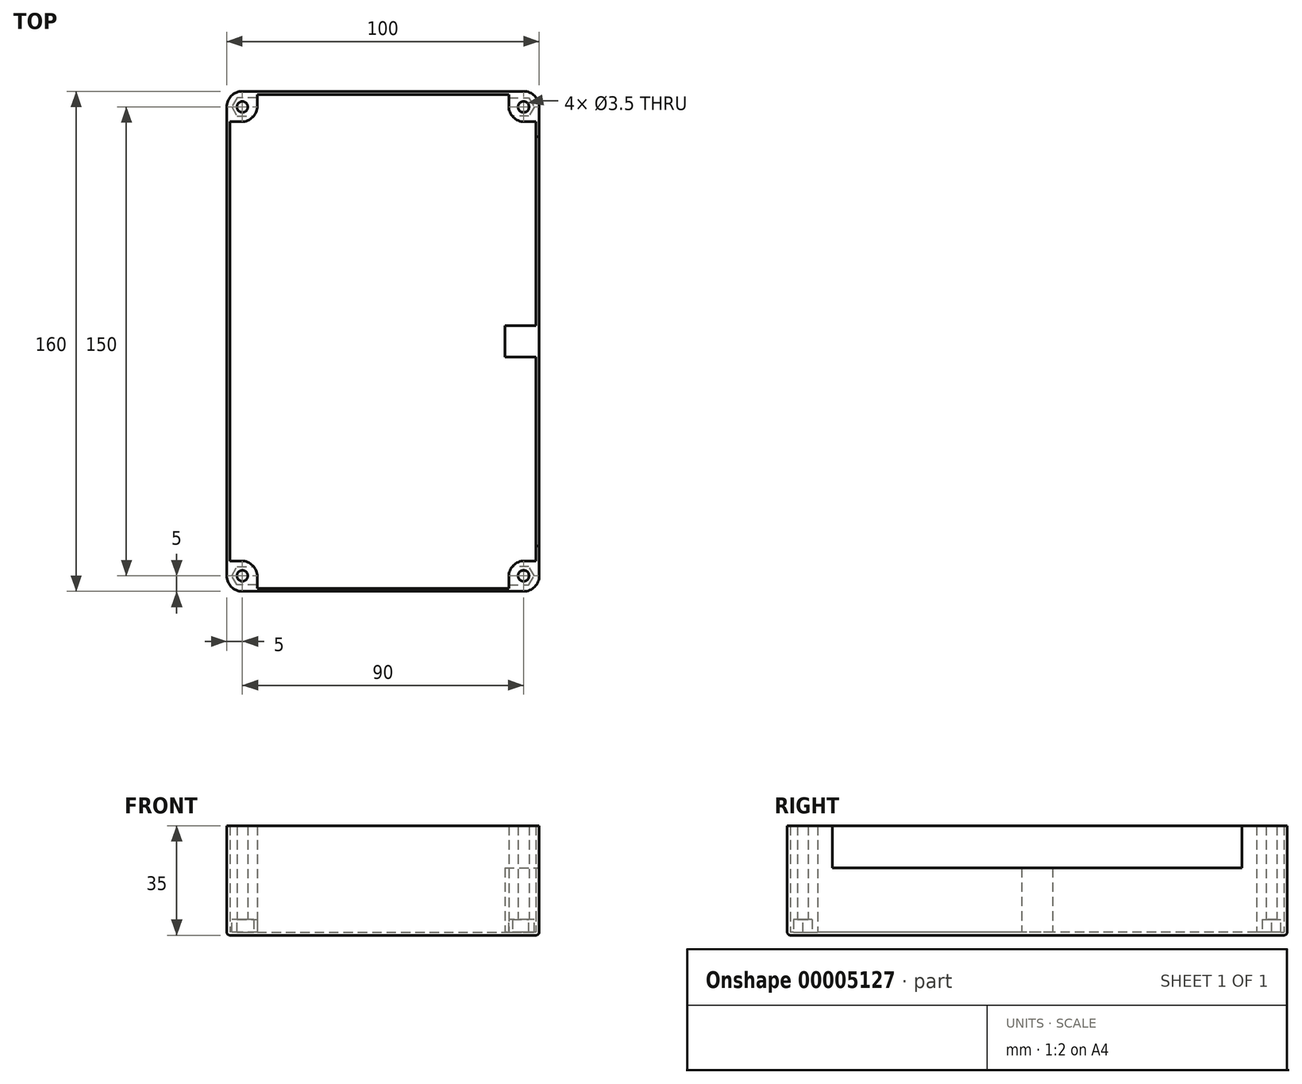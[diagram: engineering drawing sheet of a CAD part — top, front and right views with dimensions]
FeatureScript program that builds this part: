
annotation { "Feature Type Name" : "Feature", "Feature Type Description" : "" }
export const myFeature = defineFeature(function(context is Context, id is Id, definition is map)
    precondition{}
    {
        {
            var Q0;
            Q0=qCreatedBy(makeId("Top.planeOp"),FACE);
            var sketch = newSketch(context, id + "F0", { "sketchPlane" : qUnion([Q0])});
            skLineSegment(sketch, "E0.bottom", {"start": v(5, 0) * mm, "end": v(95, 0) * mm});
            skLineSegment(sketch, "E0.top", {"start": v(5, -160) * mm, "end": v(95, -160) * mm});
            skLineSegment(sketch, "E0.left", {"start": v(0, -5) * mm, "end": v(0, -155) * mm});
            skLineSegment(sketch, "E0.right", {"start": v(100, -5) * mm, "end": v(100, -155) * mm});
            skPoint(sketch, "E1.visualSharp", {"position": v(0, 0) * mm});
            skArc(sketch, "E1.filletArc", {"start": v(5, 0) * mm, "mid": v(1.46, -1.46) * mm, "end": v(0, -5) * mm});
            skPoint(sketch, "E2.visualSharp", {"position": v(0, -160) * mm});
            skArc(sketch, "E2.filletArc", {"start": v(0, -155) * mm, "mid": v(1.46, -158.54) * mm, "end": v(5, -160) * mm});
            skPoint(sketch, "E3.visualSharp", {"position": v(100, -160) * mm});
            skArc(sketch, "E3.filletArc", {"start": v(95, -160) * mm, "mid": v(98.54, -158.54) * mm, "end": v(100, -155) * mm});
            skPoint(sketch, "E4.visualSharp", {"position": v(100, 0) * mm});
            skArc(sketch, "E4.filletArc", {"start": v(100, -5) * mm, "mid": v(98.54, -1.46) * mm, "end": v(95, 0) * mm});
            skLineSegment(sketch, "E5.bottom", {"start": v(6, -1) * mm, "end": v(94, -1) * mm});
            skLineSegment(sketch, "E5.top", {"start": v(6, -159) * mm, "end": v(94, -159) * mm});
            skLineSegment(sketch, "E5.left", {"start": v(1, -6) * mm, "end": v(1, -154) * mm});
            skLineSegment(sketch, "E5.right", {"start": v(99, -6) * mm, "end": v(99, -154) * mm});
            skPoint(sketch, "E6.visualSharp", {"position": v(1, -1) * mm});
            skArc(sketch, "E6.filletArc", {"start": v(6, -1) * mm, "mid": v(2.46, -2.46) * mm, "end": v(1, -6) * mm});
            skPoint(sketch, "E7.visualSharp", {"position": v(99, -1) * mm});
            skArc(sketch, "E7.filletArc", {"start": v(99, -6) * mm, "mid": v(97.54, -2.46) * mm, "end": v(94, -1) * mm});
            skPoint(sketch, "E8.visualSharp", {"position": v(99, -159) * mm});
            skArc(sketch, "E8.filletArc", {"start": v(94, -159) * mm, "mid": v(97.54, -157.54) * mm, "end": v(99, -154) * mm});
            skPoint(sketch, "E9.visualSharp", {"position": v(1, -159) * mm});
            skArc(sketch, "E9.filletArc", {"start": v(1, -154) * mm, "mid": v(2.46, -157.54) * mm, "end": v(6, -159) * mm});
            skLineSegment(sketch, "E10", {"start": v(50, -1) * mm, "end": v(50, 0) * mm, "construction": true});
            skLineSegment(sketch, "E11", {"start": v(1, -80) * mm, "end": v(0, -80) * mm, "construction": true});
            skSolve(sketch);
        }
        {
            var Q0;
            Q0 = qSketchRegion(id + "F0", true);
            extrude(context, id + "F1", {"entities" : qUnion([Q0]), "depth" : 35 * mm});
        }
        {
            var Q0;
            Q0=qCreatedBy(makeId("Top.planeOp"),FACE);
            var sketch = newSketch(context, id + "F2", { "sketchPlane" : qUnion([Q0])});
            skLineSegment(sketch, "E12.bottom", {"start": v(5, 0) * mm, "end": v(95, 0) * mm});
            skLineSegment(sketch, "E12.top", {"start": v(5, -160) * mm, "end": v(95, -160) * mm});
            skLineSegment(sketch, "E12.left", {"start": v(0, -5) * mm, "end": v(0, -155) * mm});
            skLineSegment(sketch, "E12.right", {"start": v(100, -5) * mm, "end": v(100, -155) * mm});
            skPoint(sketch, "E13.visualSharp", {"position": v(0, 0) * mm});
            skArc(sketch, "E13.filletArc", {"start": v(5, 0) * mm, "mid": v(1.46, -1.46) * mm, "end": v(0, -5) * mm});
            skPoint(sketch, "E14.visualSharp", {"position": v(0, -160) * mm});
            skArc(sketch, "E14.filletArc", {"start": v(0, -155) * mm, "mid": v(1.46, -158.54) * mm, "end": v(5, -160) * mm});
            skPoint(sketch, "E15.visualSharp", {"position": v(100, -160) * mm});
            skArc(sketch, "E15.filletArc", {"start": v(95, -160) * mm, "mid": v(98.54, -158.54) * mm, "end": v(100, -155) * mm});
            skPoint(sketch, "E16.visualSharp", {"position": v(100, 0) * mm});
            skArc(sketch, "E16.filletArc", {"start": v(100, -5) * mm, "mid": v(98.54, -1.46) * mm, "end": v(95, 0) * mm});
            skSolve(sketch);
        }
        {
            var Q0;
            Q0 = qSketchRegion(id + "F2", true);
            extrude(context, id + "F3", {"entities" : qUnion([Q0]), "operationType" : NewBodyOperationType.ADD, "depth" : 1 * mm});
        }
        {
            var Q0;
            Q0=makeQuery(id+"F3.opExtrude","CAP_FACE",FACE,{"disambiguationData":[OSD([sQuery(id+"F2.wireOp",EDGE,"E12.bottom"),sQuery(id+"F2.wireOp",EDGE,"E12.top"),sQuery(id+"F2.wireOp",EDGE,"E12.left"),sQuery(id+"F2.wireOp",EDGE,"E12.right"),sQuery(id+"F2.wireOp",EDGE,"E13.filletArc"),sQuery(id+"F2.wireOp",EDGE,"E14.filletArc"),sQuery(id+"F2.wireOp",EDGE,"E15.filletArc"),sQuery(id+"F2.wireOp",EDGE,"E16.filletArc")])],"isStart":false});
            cPlane(context, id + "F4", {"entities" : qUnion([Q0]), "cplaneType" : CPlaneType.OFFSET, "offset" : 0 * mm, "width" : 150 * mm, "height" : 150 * mm});
        }
        {
            var Q0;
            Q0=qCreatedBy(id+"F4.planeOp",FACE);
            var sketch = newSketch(context, id + "F5", { "sketchPlane" : qUnion([Q0])});
            skLineSegment(sketch, "E17.bottom", {"start": v(4.75, -150.25) * mm, "end": v(1, -150.25) * mm});
            skLineSegment(sketch, "E17.top", {"start": v(9.75, -159) * mm, "end": v(6, -159) * mm});
            skLineSegment(sketch, "E17.left", {"start": v(9.75, -155.25) * mm, "end": v(9.75, -159) * mm});
            skLineSegment(sketch, "E17.right", {"start": v(1, -150.25) * mm, "end": v(1, -154) * mm});
            skPoint(sketch, "E18.visualSharp", {"position": v(1, -159) * mm});
            skArc(sketch, "E18.filletArc", {"start": v(1, -154) * mm, "mid": v(2.46, -157.54) * mm, "end": v(6, -159) * mm});
            skLineSegment(sketch, "E19.bottom", {"start": v(4.75, -9.75) * mm, "end": v(1, -9.75) * mm});
            skLineSegment(sketch, "E19.top", {"start": v(9.75, -1) * mm, "end": v(6, -1) * mm});
            skLineSegment(sketch, "E19.left", {"start": v(9.75, -4.75) * mm, "end": v(9.75, -1) * mm});
            skLineSegment(sketch, "E19.right", {"start": v(1, -9.75) * mm, "end": v(1, -6) * mm});
            skPoint(sketch, "E20.visualSharp", {"position": v(1, -1) * mm});
            skArc(sketch, "E20.filletArc", {"start": v(6, -1) * mm, "mid": v(2.46, -2.46) * mm, "end": v(1, -6) * mm});
            skLineSegment(sketch, "E21.bottom", {"start": v(95.25, -150.25) * mm, "end": v(99, -150.25) * mm});
            skLineSegment(sketch, "E21.top", {"start": v(90.25, -159) * mm, "end": v(94, -159) * mm});
            skLineSegment(sketch, "E21.left", {"start": v(90.25, -155.25) * mm, "end": v(90.25, -159) * mm});
            skLineSegment(sketch, "E21.right", {"start": v(99, -150.25) * mm, "end": v(99, -154) * mm});
            skLineSegment(sketch, "E22.bottom", {"start": v(95.25, -9.75) * mm, "end": v(99, -9.75) * mm});
            skLineSegment(sketch, "E22.top", {"start": v(90.25, -1) * mm, "end": v(94, -1) * mm});
            skLineSegment(sketch, "E22.left", {"start": v(90.25, -4.75) * mm, "end": v(90.25, -1) * mm});
            skLineSegment(sketch, "E22.right", {"start": v(99, -9.75) * mm, "end": v(99, -6) * mm});
            skPoint(sketch, "E23.visualSharp", {"position": v(99, -159) * mm});
            skArc(sketch, "E23.filletArc", {"start": v(94, -159) * mm, "mid": v(97.54, -157.54) * mm, "end": v(99, -154) * mm});
            skPoint(sketch, "E24.visualSharp", {"position": v(99, -1) * mm});
            skArc(sketch, "E24.filletArc", {"start": v(99, -6) * mm, "mid": v(97.54, -2.46) * mm, "end": v(94, -1) * mm});
            skCircle(sketch, "E25", {"center": v(5, -155) * mm, "radius": 1.75 * mm});
            skCircle(sketch, "E26", {"center": v(5, -5) * mm, "radius": 1.75 * mm});
            skCircle(sketch, "E27", {"center": v(95, -5) * mm, "radius": 1.75 * mm});
            skCircle(sketch, "E28", {"center": v(95, -155) * mm, "radius": 1.75 * mm});
            skLineSegment(sketch, "E29", {"start": v(5, -155) * mm, "end": v(1, -155) * mm, "construction": true});
            skLineSegment(sketch, "E30", {"start": v(95, -155) * mm, "end": v(99, -155) * mm, "construction": true});
            skLineSegment(sketch, "E31", {"start": v(5, -155) * mm, "end": v(5, -150.25) * mm, "construction": true});
            skLineSegment(sketch, "E32", {"start": v(5, -150.25) * mm, "end": v(5, -9.75) * mm, "construction": true});
            skLineSegment(sketch, "E33", {"start": v(5, -9.75) * mm, "end": v(5, -5) * mm, "construction": true});
            skPoint(sketch, "E34.visualSharp", {"position": v(9.75, -150.25) * mm});
            skArc(sketch, "E34.filletArc", {"start": v(9.75, -155.25) * mm, "mid": v(8.29, -151.71) * mm, "end": v(4.75, -150.25) * mm});
            skPoint(sketch, "E35.visualSharp", {"position": v(90.25, -150.25) * mm});
            skArc(sketch, "E35.filletArc", {"start": v(95.25, -150.25) * mm, "mid": v(91.71, -151.71) * mm, "end": v(90.25, -155.25) * mm});
            skPoint(sketch, "E36.visualSharp", {"position": v(90.25, -9.75) * mm});
            skArc(sketch, "E36.filletArc", {"start": v(90.25, -4.75) * mm, "mid": v(91.71, -8.29) * mm, "end": v(95.25, -9.75) * mm});
            skPoint(sketch, "E37.visualSharp", {"position": v(9.75, -9.75) * mm});
            skArc(sketch, "E37.filletArc", {"start": v(4.75, -9.75) * mm, "mid": v(8.29, -8.29) * mm, "end": v(9.75, -4.75) * mm});
            skLineSegment(sketch, "E38", {"start": v(5, -5) * mm, "end": v(5, -1.1) * mm, "construction": true});
            skLineSegment(sketch, "E39", {"start": v(5, -155) * mm, "end": v(5, -158.9) * mm, "construction": true});
            skSolve(sketch);
        }
        {
            var Q0;
            Q0 = qSketchRegion(id + "F5", true);
            var Q1;
            Q1=makeQuery(id+"F1.opExtrude","CAP_FACE",FACE,{"disambiguationData":[OSD([sQuery(id+"F0.wireOp",EDGE,"E0.bottom"),sQuery(id+"F0.wireOp",EDGE,"E0.top"),sQuery(id+"F0.wireOp",EDGE,"E0.left"),sQuery(id+"F0.wireOp",EDGE,"E0.right"),sQuery(id+"F0.wireOp",EDGE,"E1.filletArc"),sQuery(id+"F0.wireOp",EDGE,"E2.filletArc"),sQuery(id+"F0.wireOp",EDGE,"E3.filletArc"),sQuery(id+"F0.wireOp",EDGE,"E4.filletArc"),sQuery(id+"F0.wireOp",EDGE,"E5.bottom"),sQuery(id+"F0.wireOp",EDGE,"E5.top"),sQuery(id+"F0.wireOp",EDGE,"E5.left"),sQuery(id+"F0.wireOp",EDGE,"E5.right"),sQuery(id+"F0.wireOp",EDGE,"E6.filletArc"),sQuery(id+"F0.wireOp",EDGE,"E7.filletArc"),sQuery(id+"F0.wireOp",EDGE,"E8.filletArc"),sQuery(id+"F0.wireOp",EDGE,"E9.filletArc")])],"isStart":false});
            extrude(context, id + "F6", {"entities" : qUnion([Q0]), "operationType" : NewBodyOperationType.ADD, "endBound" : BoundingType.UP_TO_SURFACE, "endBoundEntityFace" : qUnion([Q1]), "depth" : 25 * mm});
        }
        {
            var Q0;
            Q0=qCreatedBy(makeId("Top.planeOp"),FACE);
            cPlane(context, id + "F7", {"entities" : qUnion([Q0]), "cplaneType" : CPlaneType.OFFSET, "offset" : 5 * mm, "width" : 150 * mm, "height" : 150 * mm});
        }
        {
            var Q0;
            Q0=qCreatedBy(id+"F7.planeOp",FACE);
            var sketch = newSketch(context, id + "F8", { "sketchPlane" : qUnion([Q0])});
            skCircle(sketch, "E40.cCircle", {"center": v(5, -5) * mm, "radius": 2.95 * mm, "construction": true});
            skLineSegment(sketch, "E40.0", {"start": v(3.3, -2.05) * mm, "end": v(6.7, -2.05) * mm});
            skLineSegment(sketch, "E40.3", {"start": v(6.7, -7.95) * mm, "end": v(3.3, -7.95) * mm});
            skLineSegment(sketch, "E40.4", {"start": v(3.3, -7.95) * mm, "end": v(1.6, -5) * mm});
            skLineSegment(sketch, "E40.5", {"start": v(1.6, -5) * mm, "end": v(3.3, -2.05) * mm});
            skPoint(sketch, "E40.0.midPoint", {"position": v(5, -2.05) * mm});
            skLineSegment(sketch, "E41", {"start": v(6.7, -2.05) * mm, "end": v(16.6, -2.05) * mm});
            skLineSegment(sketch, "E42", {"start": v(16.6, -2.05) * mm, "end": v(16.6, -7.95) * mm});
            skLineSegment(sketch, "E43", {"start": v(16.6, -7.95) * mm, "end": v(6.7, -7.95) * mm});
            skPoint(sketch, "E44.orphan", {"position": v(8.4, -5) * mm});
            skLineSegment(sketch, "E45", {"start": v(99, -80) * mm, "end": v(1, -80) * mm, "construction": true});
            skLineSegment(sketch, "E46", {"start": v(5, -5) * mm, "end": v(95, -5) * mm, "construction": true});
            skLineSegment(sketch, "E47", {"start": v(50, -5) * mm, "end": v(50, -91.07) * mm, "construction": true});
            skLineSegment(sketch, "E48.0.MirrorCS", {"start": v(98.4, -5) * mm, "end": v(96.7, -2.05) * mm});
            skLineSegment(sketch, "E48.1.MirrorCS", {"start": v(96.7, -2.05) * mm, "end": v(93.3, -2.05) * mm});
            skLineSegment(sketch, "E48.2.MirrorCS", {"start": v(93.3, -7.95) * mm, "end": v(96.7, -7.95) * mm});
            skCircle(sketch, "E48.3.MirrorC", {"center": v(95, -5) * mm, "radius": 2.95 * mm, "construction": true});
            skLineSegment(sketch, "E48.4.MirrorCS", {"start": v(96.7, -7.95) * mm, "end": v(98.4, -5) * mm});
            skPoint(sketch, "E48.5.MirrorP", {"position": v(95, -2.05) * mm});
            skLineSegment(sketch, "E48.6.MirrorCS", {"start": v(83.4, -2.05) * mm, "end": v(83.4, -7.95) * mm});
            skPoint(sketch, "E48.7.MirrorP", {"position": v(91.6, -5) * mm});
            skLineSegment(sketch, "E48.8.MirrorCS", {"start": v(93.3, -2.05) * mm, "end": v(83.4, -2.05) * mm});
            skLineSegment(sketch, "E48.9.MirrorCS", {"start": v(83.4, -7.95) * mm, "end": v(93.3, -7.95) * mm});
            skLineSegment(sketch, "E48.10.MirrorCS", {"start": v(95, -5) * mm, "end": v(5, -5) * mm, "construction": true});
            skLineSegment(sketch, "E49.0.MirrorCS", {"start": v(96.7, -157.95) * mm, "end": v(93.3, -157.95) * mm});
            skLineSegment(sketch, "E49.1.MirrorCS", {"start": v(93.3, -152.05) * mm, "end": v(96.7, -152.05) * mm});
            skLineSegment(sketch, "E49.2.MirrorCS", {"start": v(5, -155) * mm, "end": v(95, -155) * mm, "construction": true});
            skLineSegment(sketch, "E49.3.MirrorCS", {"start": v(3.3, -157.95) * mm, "end": v(6.7, -157.95) * mm});
            skLineSegment(sketch, "E49.4.MirrorCS", {"start": v(1.6, -155) * mm, "end": v(3.3, -157.95) * mm});
            skLineSegment(sketch, "E49.5.MirrorCS", {"start": v(96.7, -152.05) * mm, "end": v(98.4, -155) * mm});
            skLineSegment(sketch, "E49.6.MirrorCS", {"start": v(3.3, -152.05) * mm, "end": v(1.6, -155) * mm});
            skLineSegment(sketch, "E49.7.MirrorCS", {"start": v(6.7, -152.05) * mm, "end": v(3.3, -152.05) * mm});
            skCircle(sketch, "E49.8.MirrorC", {"center": v(5, -155) * mm, "radius": 2.95 * mm, "construction": true});
            skCircle(sketch, "E49.9.MirrorC", {"center": v(95, -155) * mm, "radius": 2.95 * mm, "construction": true});
            skLineSegment(sketch, "E49.10.MirrorCS", {"start": v(98.4, -155) * mm, "end": v(96.7, -157.95) * mm});
            skLineSegment(sketch, "E49.11.MirrorCS", {"start": v(6.7, -157.95) * mm, "end": v(16.6, -157.95) * mm});
            skPoint(sketch, "E49.12.MirrorP", {"position": v(95, -157.95) * mm});
            skLineSegment(sketch, "E49.13.MirrorCS", {"start": v(50, -155) * mm, "end": v(50, -68.93) * mm, "construction": true});
            skLineSegment(sketch, "E49.14.MirrorCS", {"start": v(83.4, -152.05) * mm, "end": v(93.3, -152.05) * mm});
            skLineSegment(sketch, "E49.15.MirrorCS", {"start": v(93.3, -157.95) * mm, "end": v(83.4, -157.95) * mm});
            skPoint(sketch, "E49.16.MirrorP", {"position": v(91.6, -155) * mm});
            skLineSegment(sketch, "E49.17.MirrorCS", {"start": v(95, -155) * mm, "end": v(5, -155) * mm, "construction": true});
            skLineSegment(sketch, "E49.18.MirrorCS", {"start": v(16.6, -152.05) * mm, "end": v(6.7, -152.05) * mm});
            skLineSegment(sketch, "E49.19.MirrorCS", {"start": v(83.4, -157.95) * mm, "end": v(83.4, -152.05) * mm});
            skPoint(sketch, "E49.20.MirrorP", {"position": v(8.4, -155) * mm});
            skPoint(sketch, "E49.21.MirrorP", {"position": v(5, -157.95) * mm});
            skLineSegment(sketch, "E49.22.MirrorCS", {"start": v(16.6, -157.95) * mm, "end": v(16.6, -152.05) * mm});
            skSolve(sketch);
        }
        {
            var Q0;
            Q0 = qSketchRegion(id + "F8", true);
            var Q1;
            Q1=makeQuery(id+"F6.boolean.opBoolean","SPLIT",FACE,{"disambiguationData":[TD([makeQuery(id+"F1.opExtrude","SWEPT_FACE",FACE,{"disambiguationData":[OSD([sQuery(id+"F0.wireOp",EDGE,"E5.bottom")])]})])],"derivedFrom":makeQuery(id+"F3.opExtrude","CAP_FACE",FACE,{"disambiguationData":[OSD([sQuery(id+"F2.wireOp",EDGE,"E12.bottom"),sQuery(id+"F2.wireOp",EDGE,"E12.top"),sQuery(id+"F2.wireOp",EDGE,"E12.left"),sQuery(id+"F2.wireOp",EDGE,"E12.right"),sQuery(id+"F2.wireOp",EDGE,"E13.filletArc"),sQuery(id+"F2.wireOp",EDGE,"E14.filletArc"),sQuery(id+"F2.wireOp",EDGE,"E15.filletArc"),sQuery(id+"F2.wireOp",EDGE,"E16.filletArc")])],"isStart":false})});
            extrude(context, id + "F9", {"entities" : qUnion([Q0]), "operationType" : NewBodyOperationType.REMOVE, "endBound" : BoundingType.UP_TO_SURFACE, "oppositeDirection" : true, "endBoundEntityFace" : qUnion([Q1]), "depth" : 10 * mm});
        }
        {
            var Q0;
            Q0=makeQuery(id+"F1.opExtrude","SWEPT_FACE",FACE,{"disambiguationData":[OSD([sQuery(id+"F0.wireOp",EDGE,"E0.right")])]});
            var sketch = newSketch(context, id + "F10", { "sketchPlane" : qUnion([Q0])});
            skLineSegment(sketch, "E50.bottom", {"start": v(-145.5, 35) * mm, "end": v(-14.5, 35) * mm});
            skLineSegment(sketch, "E50.top", {"start": v(-145.5, 21.5) * mm, "end": v(-14.5, 21.5) * mm});
            skLineSegment(sketch, "E50.left", {"start": v(-14.5, 35) * mm, "end": v(-14.5, 21.5) * mm});
            skLineSegment(sketch, "E50.right", {"start": v(-145.5, 35) * mm, "end": v(-145.5, 21.5) * mm});
            skLineSegment(sketch, "E51", {"start": v(-80, 21.5) * mm, "end": v(-80, 35) * mm, "construction": true});
            skSolve(sketch);
        }
        {
            var Q0;
            Q0 = qSketchRegion(id + "F10", true);
            extrude(context, id + "F11", {"entities" : qUnion([Q0]), "operationType" : NewBodyOperationType.REMOVE, "oppositeDirection" : true, "depth" : 25 * mm});
        }
        {
            var Q0;
            {var subQ0=makeQuery(id+"F3.opExtrude","CAP_FACE",FACE,{"disambiguationData":[OSD([sQuery(id+"F2.wireOp",EDGE,"E12.bottom"),sQuery(id+"F2.wireOp",EDGE,"E12.top"),sQuery(id+"F2.wireOp",EDGE,"E12.left"),sQuery(id+"F2.wireOp",EDGE,"E12.right"),sQuery(id+"F2.wireOp",EDGE,"E13.filletArc"),sQuery(id+"F2.wireOp",EDGE,"E14.filletArc"),sQuery(id+"F2.wireOp",EDGE,"E15.filletArc"),sQuery(id+"F2.wireOp",EDGE,"E16.filletArc")])],"isStart":false});Q0=makeQuery(id+"F9.boolean.opBoolean","MERGE",FACE,{"derivedFrom":[makeQuery(id+"F6.boolean.opBoolean","SPLIT",FACE,{"disambiguationData":[TD([makeQuery(id+"F1.opExtrude","SWEPT_FACE",FACE,{"disambiguationData":[OSD([sQuery(id+"F0.wireOp",EDGE,"E5.bottom")])]})])],"derivedFrom":subQ0}),makeQuery(id+"F6.boolean.opBoolean","SPLIT",FACE,{"disambiguationData":[TD([makeQuery(id+"F6.opExtrude","SWEPT_FACE",FACE,{"disambiguationData":[OSD([sQuery(id+"F5.wireOp",EDGE,"E25")])]})])],"derivedFrom":subQ0}),makeQuery(id+"F6.boolean.opBoolean","SPLIT",FACE,{"disambiguationData":[TD([makeQuery(id+"F6.opExtrude","SWEPT_FACE",FACE,{"disambiguationData":[OSD([sQuery(id+"F5.wireOp",EDGE,"E26")])]})])],"derivedFrom":subQ0}),makeQuery(id+"F6.boolean.opBoolean","SPLIT",FACE,{"disambiguationData":[TD([makeQuery(id+"F6.opExtrude","SWEPT_FACE",FACE,{"disambiguationData":[OSD([sQuery(id+"F5.wireOp",EDGE,"E27")])]})])],"derivedFrom":subQ0}),makeQuery(id+"F6.boolean.opBoolean","SPLIT",FACE,{"disambiguationData":[TD([makeQuery(id+"F6.opExtrude","SWEPT_FACE",FACE,{"disambiguationData":[OSD([sQuery(id+"F5.wireOp",EDGE,"E28")])]})])],"derivedFrom":subQ0}),makeQuery(id+"F9.opExtrude","CAP_FACE",FACE,{"disambiguationData":[OSD([sQuery(id+"F8.wireOp",EDGE,"E40.0"),sQuery(id+"F8.wireOp",EDGE,"E40.3"),sQuery(id+"F8.wireOp",EDGE,"E40.4"),sQuery(id+"F8.wireOp",EDGE,"E40.5"),sQuery(id+"F8.wireOp",EDGE,"E41"),sQuery(id+"F8.wireOp",EDGE,"E42"),sQuery(id+"F8.wireOp",EDGE,"E43")])],"isStart":false}),makeQuery(id+"F9.opExtrude","CAP_FACE",FACE,{"disambiguationData":[OSD([sQuery(id+"F8.wireOp",EDGE,"E48.0.MirrorCS"),sQuery(id+"F8.wireOp",EDGE,"E48.1.MirrorCS"),sQuery(id+"F8.wireOp",EDGE,"E48.2.MirrorCS"),sQuery(id+"F8.wireOp",EDGE,"E48.4.MirrorCS"),sQuery(id+"F8.wireOp",EDGE,"E48.6.MirrorCS"),sQuery(id+"F8.wireOp",EDGE,"E48.8.MirrorCS"),sQuery(id+"F8.wireOp",EDGE,"E48.9.MirrorCS")])],"isStart":false}),makeQuery(id+"F9.opExtrude","CAP_FACE",FACE,{"disambiguationData":[OSD([sQuery(id+"F8.wireOp",EDGE,"E49.0.MirrorCS"),sQuery(id+"F8.wireOp",EDGE,"E49.1.MirrorCS"),sQuery(id+"F8.wireOp",EDGE,"E49.5.MirrorCS"),sQuery(id+"F8.wireOp",EDGE,"E49.10.MirrorCS"),sQuery(id+"F8.wireOp",EDGE,"E49.14.MirrorCS"),sQuery(id+"F8.wireOp",EDGE,"E49.15.MirrorCS"),sQuery(id+"F8.wireOp",EDGE,"E49.19.MirrorCS")])],"isStart":false}),makeQuery(id+"F9.opExtrude","CAP_FACE",FACE,{"disambiguationData":[OSD([sQuery(id+"F8.wireOp",EDGE,"E49.3.MirrorCS"),sQuery(id+"F8.wireOp",EDGE,"E49.4.MirrorCS"),sQuery(id+"F8.wireOp",EDGE,"E49.6.MirrorCS"),sQuery(id+"F8.wireOp",EDGE,"E49.7.MirrorCS"),sQuery(id+"F8.wireOp",EDGE,"E49.11.MirrorCS"),sQuery(id+"F8.wireOp",EDGE,"E49.18.MirrorCS"),sQuery(id+"F8.wireOp",EDGE,"E49.22.MirrorCS")])],"isStart":false})]});}
            var sketch = newSketch(context, id + "F12", { "sketchPlane" : qUnion([Q0])});
            skLineSegment(sketch, "E52.bottom", {"start": v(99, -75) * mm, "end": v(89, -75) * mm});
            skLineSegment(sketch, "E52.top", {"start": v(99, -85) * mm, "end": v(89, -85) * mm});
            skLineSegment(sketch, "E52.left", {"start": v(99, -75) * mm, "end": v(99, -85) * mm});
            skLineSegment(sketch, "E52.right", {"start": v(89, -75) * mm, "end": v(89, -85) * mm});
            skLineSegment(sketch, "E53", {"start": v(99, -80) * mm, "end": v(89, -80) * mm, "construction": true});
            skSolve(sketch);
        }
        {
            var Q0;
            Q0 = qSketchRegion(id + "F12", true);
            var Q1;
            Q1=makeQuery(id+"F11.boolean.opBoolean","COPY",FACE,{"derivedFrom":makeQuery(id+"F11.opExtrude","SWEPT_FACE",FACE,{"disambiguationData":[OSD([sQuery(id+"F10.wireOp",EDGE,"E50.top")])]})});
            extrude(context, id + "F13", {"entities" : qUnion([Q0]), "operationType" : NewBodyOperationType.ADD, "endBound" : BoundingType.UP_TO_SURFACE, "endBoundEntityFace" : qUnion([Q1]), "depth" : 25 * mm});
        }
        {
            var Q0;
            Q0=makeQuery(id+"F1.opExtrude","CAP_EDGE",EDGE,{"disambiguationData":[OSD([sQuery(id+"F0.wireOp",EDGE,"E3.filletArc")])],"isStart":true});
            var Q1;
            Q1=makeQuery(id+"F1.opExtrude","CAP_EDGE",EDGE,{"disambiguationData":[OSD([sQuery(id+"F0.wireOp",EDGE,"E0.right")])],"isStart":true});
            var Q2;
            Q2=makeQuery(id+"F1.opExtrude","CAP_EDGE",EDGE,{"disambiguationData":[OSD([sQuery(id+"F0.wireOp",EDGE,"E0.top")])],"isStart":true});
            var Q3;
            Q3=makeQuery(id+"F1.opExtrude","CAP_EDGE",EDGE,{"disambiguationData":[OSD([sQuery(id+"F0.wireOp",EDGE,"E4.filletArc")])],"isStart":true});
            var Q4;
            Q4=makeQuery(id+"F1.opExtrude","CAP_EDGE",EDGE,{"disambiguationData":[OSD([sQuery(id+"F0.wireOp",EDGE,"E0.bottom")])],"isStart":true});
            var Q5;
            Q5=makeQuery(id+"F1.opExtrude","CAP_EDGE",EDGE,{"disambiguationData":[OSD([sQuery(id+"F0.wireOp",EDGE,"E1.filletArc")])],"isStart":true});
            var Q6;
            Q6=makeQuery(id+"F1.opExtrude","CAP_EDGE",EDGE,{"disambiguationData":[OSD([sQuery(id+"F0.wireOp",EDGE,"E0.left")])],"isStart":true});
            var Q7;
            Q7=makeQuery(id+"F1.opExtrude","CAP_EDGE",EDGE,{"disambiguationData":[OSD([sQuery(id+"F0.wireOp",EDGE,"E2.filletArc")])],"isStart":true});
            fillet(context, id + "F14", {"entities" : qUnion([Q0, Q1, Q2, Q3, Q4, Q5, Q6, Q7]), "radius" : 1 * mm, "tangentPropagation" : true, "allowEdgeOverflow" : false});
        }
    });
